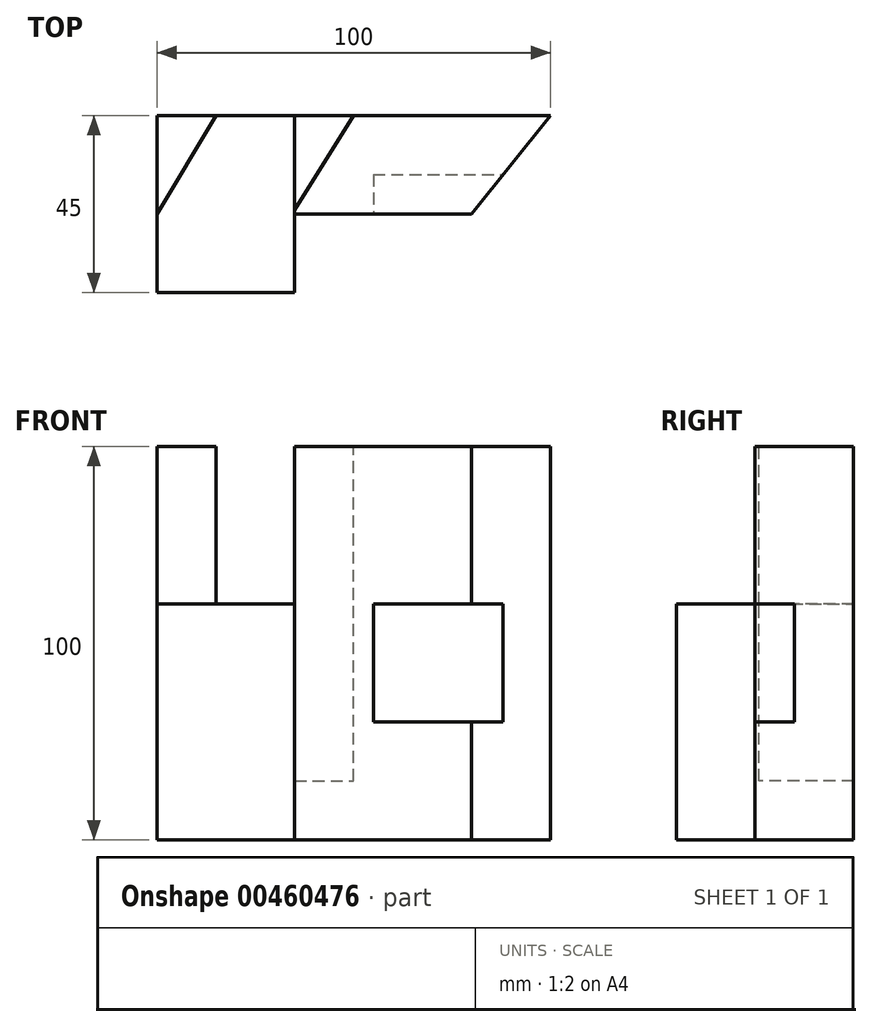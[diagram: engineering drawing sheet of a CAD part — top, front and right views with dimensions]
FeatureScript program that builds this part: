
annotation { "Feature Type Name" : "Feature", "Feature Type Description" : "" }
export const myFeature = defineFeature(function(context is Context, id is Id, definition is map)
    precondition{}
    {
        {
            var Q0;
            Q0=qCreatedBy(makeId("Top.planeOp"),FACE);
            var sketch = newSketch(context, id + "F0", { "sketchPlane" : qUnion([Q0])});
            skLineSegment(sketch, "E0.bottom", {"start": v(-54.16, -2.9) * mm, "end": v(45.84, -2.9) * mm});
            skLineSegment(sketch, "E0.top", {"start": v(-54.16, -47.9) * mm, "end": v(45.84, -47.9) * mm});
            skLineSegment(sketch, "E0.left", {"start": v(-54.16, -2.9) * mm, "end": v(-54.16, -47.9) * mm});
            skLineSegment(sketch, "E0.right", {"start": v(45.84, -2.9) * mm, "end": v(45.84, -47.9) * mm});
            skSolve(sketch);
        }
        {
            var Q0;
            Q0=makeQuery(id+"F0.imprint","IMPRINT",FACE,{"disambiguationData":[TD([[makeQuery(id+"F0.imprint","IMPRINT",EDGE,{"derivedFrom":sQuery(id+"F0.wireOp",EDGE,"E0.bottom")}),-1.0]])]});
            extrude(context, id + "F1", {"entities" : qUnion([Q0]), "depth" : 100 * mm});
        }
        {
            var Q0;
            Q0=makeQuery(id+"F1.opExtrude","CAP_FACE",FACE,{"disambiguationData":[OSD([sQuery(id+"F0.wireOp",EDGE,"E0.bottom"),sQuery(id+"F0.wireOp",EDGE,"E0.top"),sQuery(id+"F0.wireOp",EDGE,"E0.left"),sQuery(id+"F0.wireOp",EDGE,"E0.right")])],"isStart":false});
            var sketch = newSketch(context, id + "F2", { "sketchPlane" : qUnion([Q0])});
            skLineSegment(sketch, "E1.bottom", {"start": v(-54.16, -2.9) * mm, "end": v(-19.16, -2.9) * mm});
            skLineSegment(sketch, "E1.top", {"start": v(-54.16, -47.9) * mm, "end": v(-19.16, -47.9) * mm});
            skLineSegment(sketch, "E1.left", {"start": v(-54.16, -2.9) * mm, "end": v(-54.16, -47.9) * mm});
            skLineSegment(sketch, "E1.right", {"start": v(-19.16, -2.9) * mm, "end": v(-19.16, -47.9) * mm});
            skSolve(sketch);
        }
        {
            var Q0;
            Q0=makeQuery(id+"F2.imprint","IMPRINT",FACE,{"disambiguationData":[TD([[makeQuery(id+"F2.imprint","IMPRINT",EDGE,{"derivedFrom":sQuery(id+"F2.wireOp",EDGE,"E1.bottom")}),-1.0]])]});
            extrude(context, id + "F3", {"entities" : qUnion([Q0]), "operationType" : NewBodyOperationType.REMOVE, "oppositeDirection" : true, "depth" : 40 * mm});
        }
        {
            var Q0;
            Q0=makeQuery(id+"F3.boolean.opBoolean","COPY",FACE,{"derivedFrom":makeQuery(id+"F3.opExtrude","CAP_FACE",FACE,{"disambiguationData":[OSD([sQuery(id+"F2.wireOp",EDGE,"E1.bottom"),sQuery(id+"F2.wireOp",EDGE,"E1.top"),sQuery(id+"F2.wireOp",EDGE,"E1.left"),sQuery(id+"F2.wireOp",EDGE,"E1.right")])],"isStart":false})});
            var sketch = newSketch(context, id + "F4", { "sketchPlane" : qUnion([Q0])});
            skLineSegment(sketch, "E2", {"start": v(-54.16, -2.9) * mm, "end": v(-54.16, -27.9) * mm});
            skLineSegment(sketch, "E3", {"start": v(-54.16, -27.9) * mm, "end": v(-39.16, -2.9) * mm});
            skLineSegment(sketch, "E4", {"start": v(-39.16, -2.9) * mm, "end": v(-54.16, -2.9) * mm});
            skSolve(sketch);
        }
        {
            var Q0;
            Q0=makeQuery(id+"F4.imprint","IMPRINT",FACE,{"disambiguationData":[TD([[makeQuery(id+"F4.imprint","IMPRINT",EDGE,{"derivedFrom":sQuery(id+"F4.wireOp",EDGE,"E2")}),1.0]])]});
            extrude(context, id + "F5", {"entities" : qUnion([Q0]), "operationType" : NewBodyOperationType.ADD, "depth" : 40 * mm});
        }
        {
            var Q0;
            Q0=makeQuery(id+"F1.opExtrude","CAP_FACE",FACE,{"disambiguationData":[OSD([sQuery(id+"F0.wireOp",EDGE,"E0.bottom"),sQuery(id+"F0.wireOp",EDGE,"E0.top"),sQuery(id+"F0.wireOp",EDGE,"E0.left"),sQuery(id+"F0.wireOp",EDGE,"E0.right")])],"isStart":false});
            var sketch = newSketch(context, id + "F6", { "sketchPlane" : qUnion([Q0])});
            skLineSegment(sketch, "E5.bottom", {"start": v(-19.16, -27.9) * mm, "end": v(45.84, -27.9) * mm});
            skLineSegment(sketch, "E5.top", {"start": v(-19.16, -47.9) * mm, "end": v(45.84, -47.9) * mm});
            skLineSegment(sketch, "E5.left", {"start": v(-19.16, -27.9) * mm, "end": v(-19.16, -47.9) * mm});
            skLineSegment(sketch, "E5.right", {"start": v(45.84, -27.9) * mm, "end": v(45.84, -47.9) * mm});
            skSolve(sketch);
        }
        {
            var Q0;
            Q0=makeQuery(id+"F6.imprint","IMPRINT",FACE,{"disambiguationData":[TD([[makeQuery(id+"F6.imprint","IMPRINT",EDGE,{"derivedFrom":sQuery(id+"F6.wireOp",EDGE,"E5.bottom")}),-1.0]])]});
            extrude(context, id + "F7", {"entities" : qUnion([Q0]), "operationType" : NewBodyOperationType.REMOVE, "oppositeDirection" : true, "depth" : 100 * mm});
        }
        {
            var Q0;
            Q0=makeQuery(id+"F1.opExtrude","CAP_FACE",FACE,{"disambiguationData":[OSD([sQuery(id+"F0.wireOp",EDGE,"E0.bottom"),sQuery(id+"F0.wireOp",EDGE,"E0.top"),sQuery(id+"F0.wireOp",EDGE,"E0.left"),sQuery(id+"F0.wireOp",EDGE,"E0.right")])],"isStart":false});
            var sketch = newSketch(context, id + "F8", { "sketchPlane" : qUnion([Q0])});
            skLineSegment(sketch, "E6", {"start": v(-4.16, -2.9) * mm, "end": v(-19.16, -26.9) * mm});
            skLineSegment(sketch, "E7", {"start": v(-19.16, -26.9) * mm, "end": v(-19.16, -2.9) * mm});
            skLineSegment(sketch, "E8", {"start": v(-19.16, -2.9) * mm, "end": v(-4.16, -2.9) * mm});
            skSolve(sketch);
        }
        {
            var Q0;
            Q0=makeQuery(id+"F8.imprint","IMPRINT",FACE,{"disambiguationData":[TD([[makeQuery(id+"F8.imprint","IMPRINT",EDGE,{"derivedFrom":sQuery(id+"F8.wireOp",EDGE,"E6")}),-1.0]])]});
            extrude(context, id + "F9", {"entities" : qUnion([Q0]), "operationType" : NewBodyOperationType.REMOVE, "oppositeDirection" : true, "depth" : 85 * mm});
        }
        {
            var Q0;
            Q0=makeQuery(id+"F1.opExtrude","CAP_FACE",FACE,{"disambiguationData":[OSD([sQuery(id+"F0.wireOp",EDGE,"E0.bottom"),sQuery(id+"F0.wireOp",EDGE,"E0.top"),sQuery(id+"F0.wireOp",EDGE,"E0.left"),sQuery(id+"F0.wireOp",EDGE,"E0.right")])],"isStart":false});
            var sketch = newSketch(context, id + "F10", { "sketchPlane" : qUnion([Q0])});
            skLineSegment(sketch, "E9", {"start": v(45.84, -27.9) * mm, "end": v(25.84, -27.9) * mm});
            skLineSegment(sketch, "E10", {"start": v(25.84, -27.9) * mm, "end": v(45.84, -2.9) * mm});
            skLineSegment(sketch, "E11", {"start": v(45.84, -2.9) * mm, "end": v(45.84, -27.9) * mm});
            skSolve(sketch);
        }
        {
            var Q0;
            Q0=makeQuery(id+"F7.boolean.opBoolean","COPY",FACE,{"derivedFrom":makeQuery(id+"F7.opExtrude","SWEPT_FACE",FACE,{"disambiguationData":[OSD([sQuery(id+"F6.wireOp",EDGE,"E5.bottom")])]})});
            var sketch = newSketch(context, id + "F11", { "sketchPlane" : qUnion([Q0])});
            skLineSegment(sketch, "E12.bottom", {"start": v(0.84, 60) * mm, "end": v(40.53, 60) * mm});
            skLineSegment(sketch, "E12.top", {"start": v(0.84, 30) * mm, "end": v(40.53, 30) * mm});
            skLineSegment(sketch, "E12.left", {"start": v(0.84, 60) * mm, "end": v(0.84, 30) * mm});
            skLineSegment(sketch, "E12.right", {"start": v(40.53, 60) * mm, "end": v(40.53, 30) * mm});
            skSolve(sketch);
        }
        {
            var Q0;
            Q0 = qSketchRegion(id + "F11", true);
            extrude(context, id + "F12", {"entities" : qUnion([Q0]), "operationType" : NewBodyOperationType.REMOVE, "oppositeDirection" : true, "depth" : 10 * mm});
        }
        {
            var Q0;
            Q0=makeQuery(id+"F10.imprint","IMPRINT",FACE,{"disambiguationData":[TD([[makeQuery(id+"F10.imprint","IMPRINT",EDGE,{"derivedFrom":sQuery(id+"F10.wireOp",EDGE,"E9")}),1.0]])]});
            extrude(context, id + "F13", {"entities" : qUnion([Q0]), "operationType" : NewBodyOperationType.REMOVE, "oppositeDirection" : true, "depth" : 100 * mm});
        }
    });
